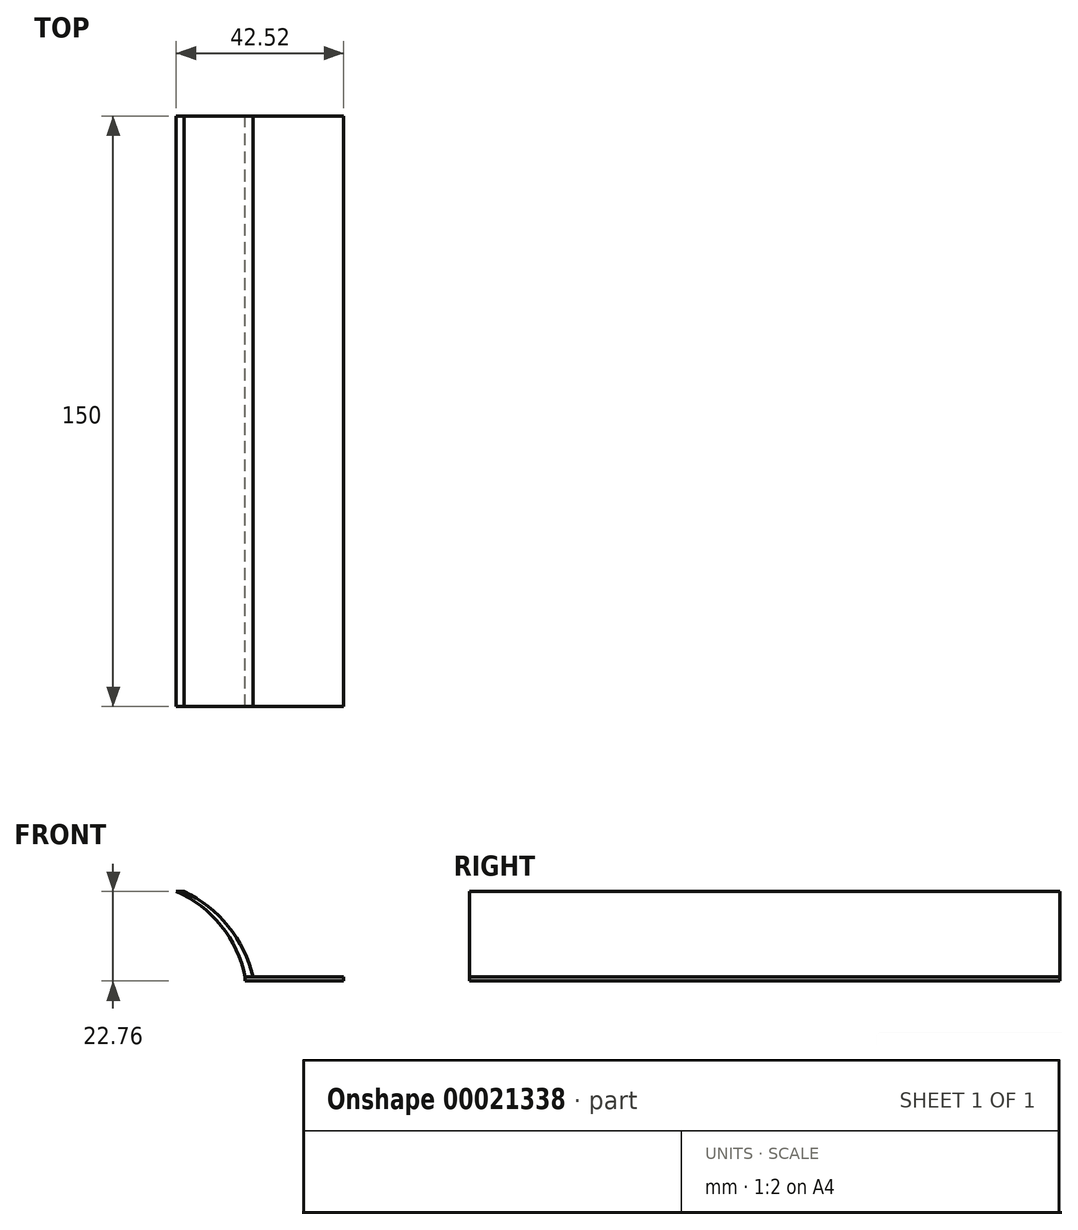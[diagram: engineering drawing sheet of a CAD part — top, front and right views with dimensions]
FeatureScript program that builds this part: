
annotation { "Feature Type Name" : "Feature", "Feature Type Description" : "" }
export const myFeature = defineFeature(function(context is Context, id is Id, definition is map)
    precondition{}
    {
        {
            var Q0;
            Q0=qCreatedBy(makeId("Front.planeOp"),FACE);
            var sketch = newSketch(context, id + "F0", { "sketchPlane" : qUnion([Q0])});
            skLineSegment(sketch, "E0", {"start": v(-22.1, 1) * mm, "end": v(-20.1, 1.02) * mm});
            skLineSegment(sketch, "E1.bottom", {"start": v(-22.1, 1) * mm, "end": v(2.9, 1) * mm});
            skLineSegment(sketch, "E1.top", {"start": v(-22.1, 0) * mm, "end": v(2.9, 0) * mm});
            skLineSegment(sketch, "E1.left", {"start": v(-22.1, 1) * mm, "end": v(-22.1, 0) * mm});
            skLineSegment(sketch, "E1.right", {"start": v(2.9, 1) * mm, "end": v(2.9, 0) * mm});
            skArc(sketch, "E2", {"start": v(-22.1, 1) * mm, "mid": v(-28.19, 14.05) * mm, "end": v(-39.63, 22.75) * mm});
            skArc(sketch, "E3", {"start": v(-20.1, 1.02) * mm, "mid": v(-26.4, 13.87) * mm, "end": v(-37.63, 22.76) * mm});
            skLineSegment(sketch, "E4", {"start": v(-39.63, 22.75) * mm, "end": v(-37.63, 22.76) * mm});
            skSolve(sketch);
        }
        {
            var Q0;
            Q0=makeQuery(id+"F0.imprint","IMPRINT",FACE,{"disambiguationData":[TD([[makeQuery(id+"F0.imprint","IMPRINT",EDGE,{"derivedFrom":sQuery(id+"F0.wireOp",EDGE,"E2")}),-1.0]])]});
            var Q1;
            Q1=makeQuery(id+"F0.imprint","IMPRINT",FACE,{"disambiguationData":[TD([[makeQuery(id+"F0.imprint","IMPRINT",EDGE,{"derivedFrom":sQuery(id+"F0.wireOp",EDGE,"E1.bottom")}),-1.0]])]});
            extrude(context, id + "F1", {"entities" : qUnion([Q0, Q1]), "endBound" : BoundingType.SYMMETRIC, "depth" : 150 * mm});
        }
    });
